# Revit family: Shower-Valve-KOHLER-Aqua_Turbo-K-880IN
name_source: partatom
category: Plumbing Fixtures
revit_build: Autodesk Revit 2017 (Build: 20160225_1515(x64)
units: mm (PartAtom-declared; Revit-internal decimal feet)

## family parameters
Cut with Voids When Loaded = No
Host = Face
OmniClass Number = 23.31.17.00
OmniClass Title = Showers
Part Type = Normal
Room Calculation Point = No
Round Connector Dimension = Use Diameter
Shared = No

## types (5) — shared parameters
ADA Compliant = No
Assembly Code = D2010700
CW Connection = Yes
Cold Water Inlet = Cold Water Inlet
Date Modified = 09/11/2020
Description = Single-Control recessed shower only valve
Drain Included = No
Flow Rate = 0 GPM
HW Connection = Yes
Height = 6 1/2"
Hot Water Inlet = Hot Water Inlet
Length = 5 3/8"
Manufacturer = KOHLER Co.
Master Format 2014 = 22 42 23
Master Format 2014 Name = Residential Showers
Material = Premium Metal construction
Pressure = 0.00 psi
Product Documentation Link = http://resources.kohler.com
Product Name = Aqua Turbo
Product Page URL = https://www.kohler.co.in
Tempered water outlet 2 = Tempered water outlet 2
Tempered watet outlet 1 = Tempered watet outlet 1
URL = https://www.kohler.co.in
Vent Connection = No
Waste Connection = No
Waste Water Outlet = Waste Water Outlet
WaterSense Certified = No
Width = 3 7/16"

## per-type parameters (varying)
| type | Default Elevation | Finish | Model | Type |
| CP- Polished Chrome | 42" | Kohler-Metal-CP-Polished_Chrome | K-880IN-CP | 1 |
| RGD-Rose Gold | 48 1/16" | Kohler-Metal-RGD-Rose_Gold | K-880IN-RGD | 2 |
| BN-Brushed Nickel | 48 1/16" | Kohler-Metal-BN-Vibrant_Brushed_Nickel | K-880IN-BN | 3 |
| BV-Brushed Bronze | 48 1/16" | Kohler-Metal-BV-Brushed_Bronze | K-880IN-BV | 4 |
| AF-French Gold | 48 1/16" | Kohler-Metal-AF-Vibrant_French_Gold | K-880IN-AF | 5 |

## geometry (parser evidence)
native form markers: Sweep x5
no freeform markers — native parametric forms only
